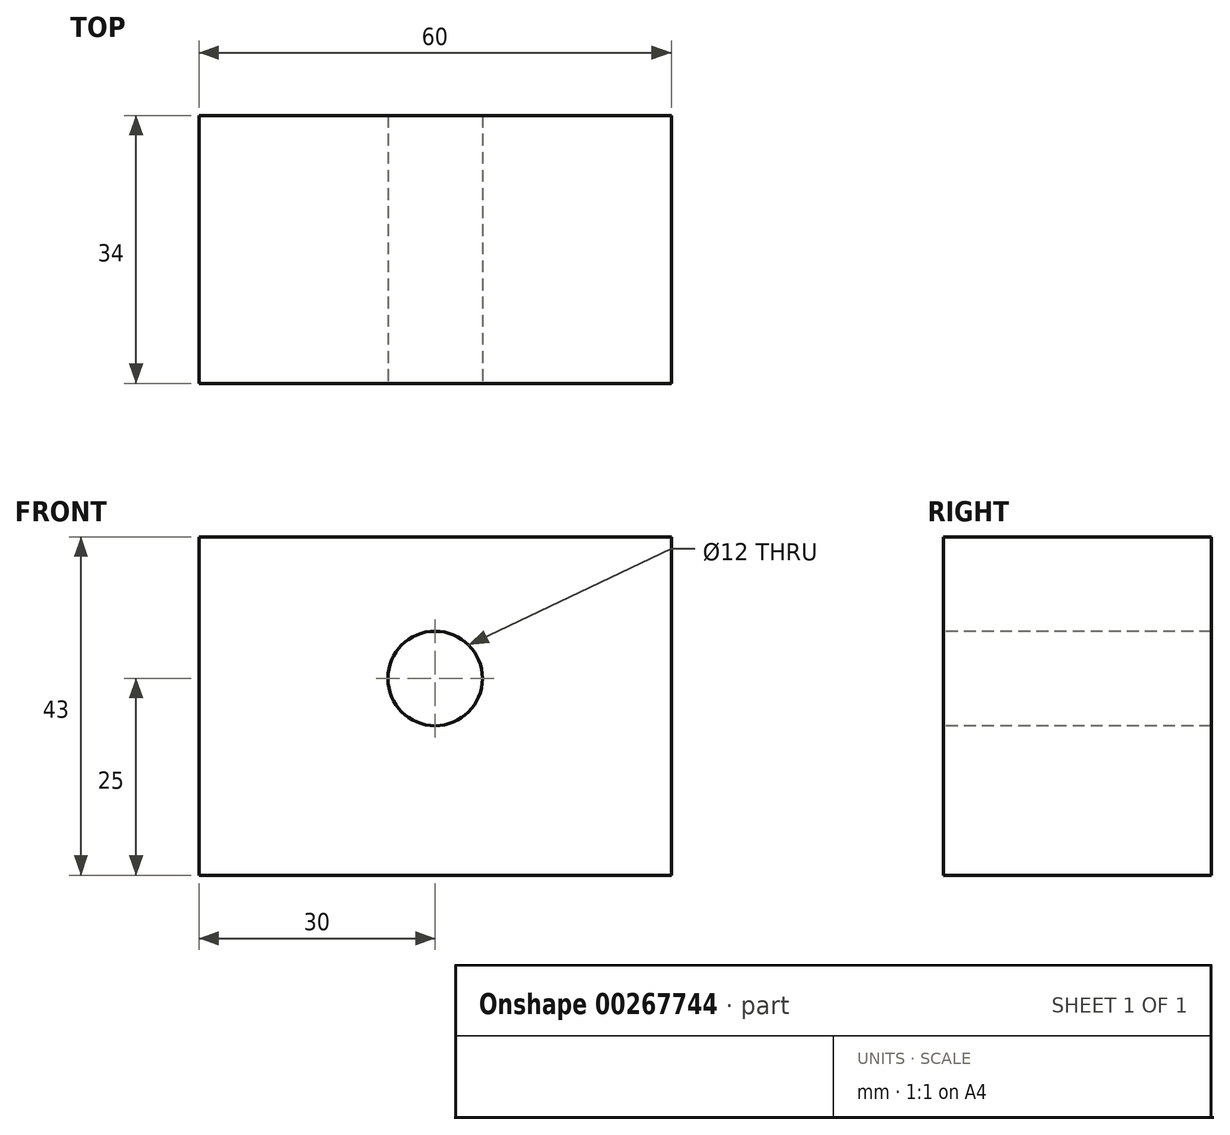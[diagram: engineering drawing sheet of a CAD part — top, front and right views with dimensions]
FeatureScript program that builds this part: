
annotation { "Feature Type Name" : "Feature", "Feature Type Description" : "" }
export const myFeature = defineFeature(function(context is Context, id is Id, definition is map)
    precondition{}
    {
        {
            var Q0;
            Q0=qCreatedBy(makeId("Front.planeOp"),FACE);
            var sketch = newSketch(context, id + "F0", { "sketchPlane" : qUnion([Q0])});
            skLineSegment(sketch, "E0.bottom", {"start": v(30, 21.5) * mm, "end": v(-30, 21.5) * mm});
            skLineSegment(sketch, "E0.top", {"start": v(30, -21.5) * mm, "end": v(-30, -21.5) * mm});
            skLineSegment(sketch, "E0.left", {"start": v(30, 21.5) * mm, "end": v(30, -21.5) * mm});
            skLineSegment(sketch, "E0.right", {"start": v(-30, 21.5) * mm, "end": v(-30, -21.5) * mm});
            skPoint(sketch, "E0.middle", {"position": v(0, 0) * mm});
            skLineSegment(sketch, "E1", {"start": v(0, -21.5) * mm, "end": v(0, 3.5) * mm, "construction": true});
            skCircle(sketch, "E2", {"center": v(0, 3.5) * mm, "radius": 6 * mm});
            skSolve(sketch);
        }
        {
            var Q0;
            Q0=makeQuery(id+"F0.imprint","IMPRINT",FACE,{"disambiguationData":[TD([[makeQuery(id+"F0.imprint","IMPRINT",EDGE,{"derivedFrom":sQuery(id+"F0.wireOp",EDGE,"E0.bottom")}),1.0]])]});
            extrude(context, id + "F1", {"entities" : qUnion([Q0]), "oppositeDirection" : true, "depth" : 34 * mm});
        }
    });
